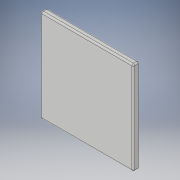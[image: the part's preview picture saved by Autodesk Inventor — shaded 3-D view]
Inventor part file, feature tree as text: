
AUTODESK INVENTOR PART (.ipt)
format: ipt  version: 2019 (Build 230136000, 136)  size: 106,496 bytes
history: native  units: in
note: dims shown in document units (in); Inventor stores cm internally (conversion verified against a paired STEP export)
features: extrude x1, fillet x1, sketch x1
ambient origin geometry x8: Origin, YZ Plane, XZ Plane, XY Plane, X Axis, Y Axis, Z Axis, Center Point
bodies: Solid1 (feature_tree)
feature tree (3):
  extrude  "Extrusion1"  Depth=5.9055in
  fillet  "Fillet1"  Radius=0.3937in
  sketch  "Sketch1"  dims[d0=5.9055in d1=5.9055in d2=0.3937in d3=0.0in d4=0.0984in]
